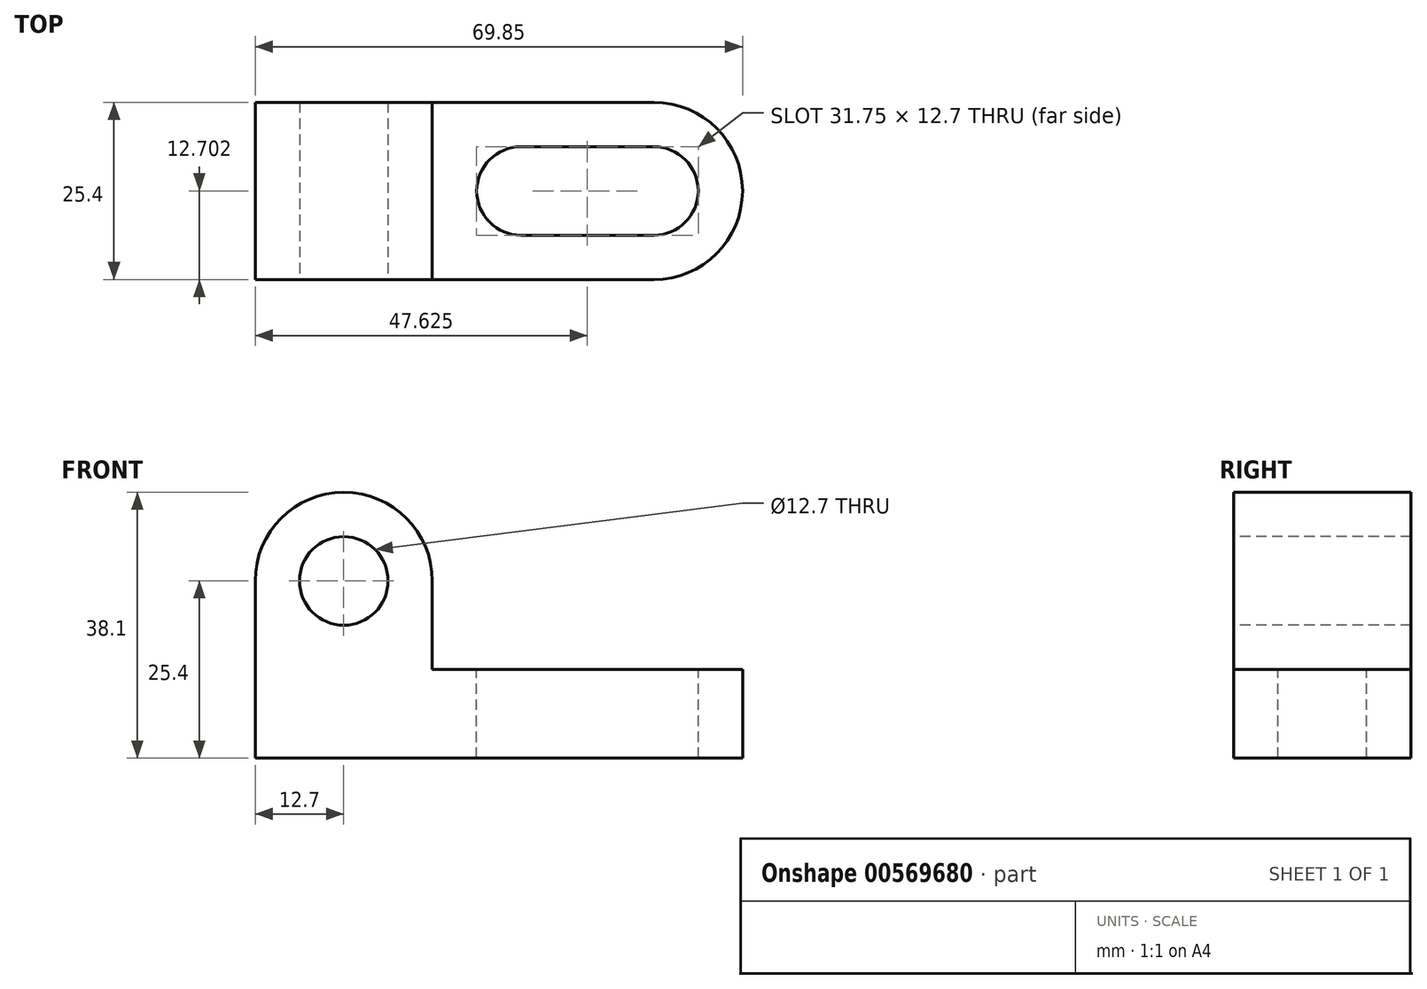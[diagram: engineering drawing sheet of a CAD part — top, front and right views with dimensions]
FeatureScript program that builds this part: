
annotation { "Feature Type Name" : "Feature", "Feature Type Description" : "" }
export const myFeature = defineFeature(function(context is Context, id is Id, definition is map)
    precondition{}
    {
        {
            var Q0;
            Q0=qCreatedBy(makeId("Top.planeOp"),FACE);
            var sketch = newSketch(context, id + "F0", { "sketchPlane" : qUnion([Q0])});
            skLineSegment(sketch, "E0.bottom", {"start": v(-34.15, -24.42) * mm, "end": v(35.7, -24.42) * mm});
            skLineSegment(sketch, "E0.top", {"start": v(-34.15, 0.98) * mm, "end": v(35.7, 0.98) * mm});
            skLineSegment(sketch, "E0.left", {"start": v(-34.15, -24.42) * mm, "end": v(-34.15, 0.98) * mm});
            skLineSegment(sketch, "E0.right", {"start": v(35.7, -24.42) * mm, "end": v(35.7, 0.98) * mm});
            skSolve(sketch);
        }
        {
            var Q0;
            Q0 = qSketchRegion(id + "F0", true);
            extrude(context, id + "F1", {"entities" : qUnion([Q0]), "depth" : 38.1 * mm, "offsetDistance" : 25.4 * mm});
        }
        {
            var Q0;
            Q0=makeQuery(id+"F1.opExtrude","SWEPT_FACE",FACE,{"disambiguationData":[OSD([sQuery(id+"F0.wireOp",EDGE,"E0.bottom")])]});
            var sketch = newSketch(context, id + "F2", { "sketchPlane" : qUnion([Q0])});
            skLineSegment(sketch, "E1", {"start": v(-8.75, 38.1) * mm, "end": v(-8.75, 12.7) * mm});
            skLineSegment(sketch, "E2", {"start": v(-8.75, 12.7) * mm, "end": v(35.7, 12.7) * mm});
            skLineSegment(sketch, "E3", {"start": v(35.7, 12.7) * mm, "end": v(35.7, 38.1) * mm});
            skLineSegment(sketch, "E4", {"start": v(35.7, 38.1) * mm, "end": v(-8.75, 38.1) * mm});
            skSolve(sketch);
        }
        {
            var Q0;
            Q0 = qSketchRegion(id + "F2", true);
            extrude(context, id + "F3", {"entities" : qUnion([Q0]), "operationType" : NewBodyOperationType.REMOVE, "oppositeDirection" : true, "depth" : 25.4 * mm, "offsetDistance" : 25.4 * mm});
        }
        {
            var Q0;
            Q0=makeQuery(id+"F1.opExtrude","SWEPT_FACE",FACE,{"disambiguationData":[OSD([sQuery(id+"F0.wireOp",EDGE,"E0.bottom")])]});
            var sketch = newSketch(context, id + "F4", { "sketchPlane" : qUnion([Q0])});
            skCircle(sketch, "E5", {"center": v(-21.45, 25.4) * mm, "radius": 6.35 * mm});
            skPoint(sketch, "E6.start.orphan", {"position": v(-21.45, 38.1) * mm});
            skPoint(sketch, "E7.end.orphan", {"position": v(-8.75, 25.4) * mm});
            skSolve(sketch);
        }
        {
            var Q0;
            Q0=makeQuery(id+"F4.imprint","IMPRINT",FACE,{"disambiguationData":[TD([[makeQuery(id+"F4.imprint","IMPRINT",EDGE,{"derivedFrom":sQuery(id+"F4.wireOp",EDGE,"E5")}),1.0]])]});
            extrude(context, id + "F5", {"entities" : qUnion([Q0]), "operationType" : NewBodyOperationType.REMOVE, "oppositeDirection" : true, "depth" : 25.4 * mm, "offsetDistance" : 25.4 * mm});
        }
        {
            var Q0;
            Q0=makeQuery(id+"F1.opExtrude","SWEPT_FACE",FACE,{"disambiguationData":[OSD([sQuery(id+"F0.wireOp",EDGE,"E0.bottom")])]});
            var sketch = newSketch(context, id + "F6", { "sketchPlane" : qUnion([Q0])});
            skLineSegment(sketch, "E8", {"start": v(-34.15, 38.1) * mm, "end": v(-34.15, 25.4) * mm});
            skArc(sketch, "E9", {"start": v(-8.75, 25.4) * mm, "mid": v(-21.45, 38.1) * mm, "end": v(-34.15, 25.4) * mm});
            skSolve(sketch);
        }
        {
            var Q0;
            {var subQ0=sQuery(id+"F6.wireOp",EDGE,"E8");Q0=makeQuery(id+"F6.imprint","IMPRINT",FACE,{"disambiguationData":[TD([[makeQuery(id+"F6.imprint","IMPRINT",EDGE,{"derivedFrom":subQ0}),1.0]])]});}
            var Q1;
            {var subQ0=sQuery(id+"F6.wireOp",EDGE,"E9");var subQ1=makeQuery(id+"F3.boolean.opBoolean","COPY",EDGE,{"derivedFrom":makeQuery(id+"F3.opExtrude","CAP_EDGE",EDGE,{"disambiguationData":[OSD([sQuery(id+"F2.wireOp",EDGE,"E1")])],"isStart":true})});var subQ2=makeQuery(id+"F6.imprint","INTERSECT",VERTEX,{"derivedFrom":[subQ1,subQ0]});Q1=makeQuery(id+"F6.imprint","IMPRINT",FACE,{"disambiguationData":[TD([[makeQuery(id+"F6.imprint","IMPRINT",EDGE,{"disambiguationData":[TD([[subQ2,-1.0]])],"derivedFrom":subQ0}),-1.0]])]});}
            extrude(context, id + "F7", {"entities" : qUnion([Q0, Q1]), "operationType" : NewBodyOperationType.REMOVE, "oppositeDirection" : true, "depth" : 25.4 * mm, "offsetDistance" : 25.4 * mm});
        }
        {
            var Q0;
            Q0=makeQuery(id+"F3.boolean.opBoolean","COPY",FACE,{"derivedFrom":makeQuery(id+"F3.opExtrude","SWEPT_FACE",FACE,{"disambiguationData":[OSD([sQuery(id+"F2.wireOp",EDGE,"E2")])]})});
            var sketch = newSketch(context, id + "F8", { "sketchPlane" : qUnion([Q0])});
            skCircle(sketch, "E10", {"center": v(23, -11.72) * mm, "radius": 6.35 * mm});
            skPoint(sketch, "E11.center.orphan", {"position": v(-2.4, -11.72) * mm});
            skPoint(sketch, "E12.end.orphan", {"position": v(-2.4, 0.98) * mm});
            skPoint(sketch, "E13.start.orphan", {"position": v(-2.4, -24.42) * mm});
            skCircle(sketch, "E14", {"center": v(3.95, -11.72) * mm, "radius": 6.35 * mm});
            skPoint(sketch, "E15.start.orphan", {"position": v(23, 0.98) * mm});
            skPoint(sketch, "E16.trimOffspring.end.orphan", {"position": v(23, -24.42) * mm});
            skPoint(sketch, "E17.trimOffspring.end.orphan", {"position": v(3.95, -24.42) * mm});
            skPoint(sketch, "E18.end.orphan", {"position": v(3.95, 0.98) * mm});
            skSolve(sketch);
        }
        {
            var Q0;
            Q0=makeQuery(id+"F8.imprint","IMPRINT",FACE,{"disambiguationData":[TD([[makeQuery(id+"F8.imprint","IMPRINT",EDGE,{"derivedFrom":sQuery(id+"F8.wireOp",EDGE,"E10")}),1.0]])]});
            var Q1;
            Q1=makeQuery(id+"F8.imprint","IMPRINT",FACE,{"disambiguationData":[TD([[makeQuery(id+"F8.imprint","IMPRINT",EDGE,{"derivedFrom":sQuery(id+"F8.wireOp",EDGE,"E14")}),1.0]])]});
            extrude(context, id + "F9", {"entities" : qUnion([Q0, Q1]), "operationType" : NewBodyOperationType.REMOVE, "oppositeDirection" : true, "depth" : 12.7 * mm, "offsetDistance" : 25.4 * mm});
        }
        {
            var Q0;
            Q0=makeQuery(id+"F3.boolean.opBoolean","COPY",FACE,{"derivedFrom":makeQuery(id+"F3.opExtrude","SWEPT_FACE",FACE,{"disambiguationData":[OSD([sQuery(id+"F2.wireOp",EDGE,"E2")])]})});
            var sketch = newSketch(context, id + "F10", { "sketchPlane" : qUnion([Q0])});
            skLineSegment(sketch, "E19", {"start": v(23, -18.07) * mm, "end": v(3.95, -18.07) * mm});
            skLineSegment(sketch, "E20", {"start": v(3.95, -5.37) * mm, "end": v(23, -5.37) * mm});
            skPoint(sketch, "E21.end.orphan", {"position": v(23, -11.72) * mm});
            skSolve(sketch);
        }
        {
            var Q0;
            {var subQ0=sQuery(id+"F10.wireOp",EDGE,"E19");Q0=makeQuery(id+"F10.imprint","IMPRINT",FACE,{"disambiguationData":[TD([[makeQuery(id+"F10.imprint","IMPRINT",EDGE,{"derivedFrom":subQ0}),-1.0]])]});}
            extrude(context, id + "F11", {"entities" : qUnion([Q0]), "operationType" : NewBodyOperationType.REMOVE, "oppositeDirection" : true, "depth" : 12.7 * mm, "offsetDistance" : 25.4 * mm});
        }
        {
            var Q0;
            Q0=makeQuery(id+"F3.boolean.opBoolean","COPY",FACE,{"derivedFrom":makeQuery(id+"F3.opExtrude","SWEPT_FACE",FACE,{"disambiguationData":[OSD([sQuery(id+"F2.wireOp",EDGE,"E2")])]})});
            var sketch = newSketch(context, id + "F12", { "sketchPlane" : qUnion([Q0])});
            skLineSegment(sketch, "E22", {"start": v(35.7, -24.42) * mm, "end": v(23, -24.42) * mm});
            skArc(sketch, "E23", {"start": v(23, -24.42) * mm, "mid": v(35.7, -11.72) * mm, "end": v(23, 0.98) * mm});
            skPoint(sketch, "E24.end.orphan", {"position": v(23, 0.98) * mm});
            skSolve(sketch);
        }
        {
            var Q0;
            {var subQ0=sQuery(id+"F12.wireOp",EDGE,"E23");var subQ1=sQuery(id+"F2.wireOp",EDGE,"E2");var subQ2=makeQuery(id+"F3.boolean.opBoolean","COPY",EDGE,{"derivedFrom":makeQuery(id+"F3.opExtrude","CAP_EDGE",EDGE,{"disambiguationData":[OSD([subQ1])],"isStart":false})});var subQ3=makeQuery(id+"F12.imprint","INTERSECT",VERTEX,{"derivedFrom":[subQ2,subQ0]});Q0=makeQuery(id+"F12.imprint","IMPRINT",FACE,{"disambiguationData":[TD([[makeQuery(id+"F12.imprint","IMPRINT",EDGE,{"disambiguationData":[TD([[subQ3,1.0]])],"derivedFrom":subQ0}),-1.0]])]});}
            var Q1;
            {var subQ0=sQuery(id+"F12.wireOp",EDGE,"E22");Q1=makeQuery(id+"F12.imprint","IMPRINT",FACE,{"disambiguationData":[TD([[makeQuery(id+"F12.imprint","IMPRINT",EDGE,{"derivedFrom":subQ0}),1.0]])]});}
            extrude(context, id + "F13", {"entities" : qUnion([Q0, Q1]), "operationType" : NewBodyOperationType.REMOVE, "oppositeDirection" : true, "depth" : 25.4 * mm, "offsetDistance" : 25.4 * mm});
        }
    });
